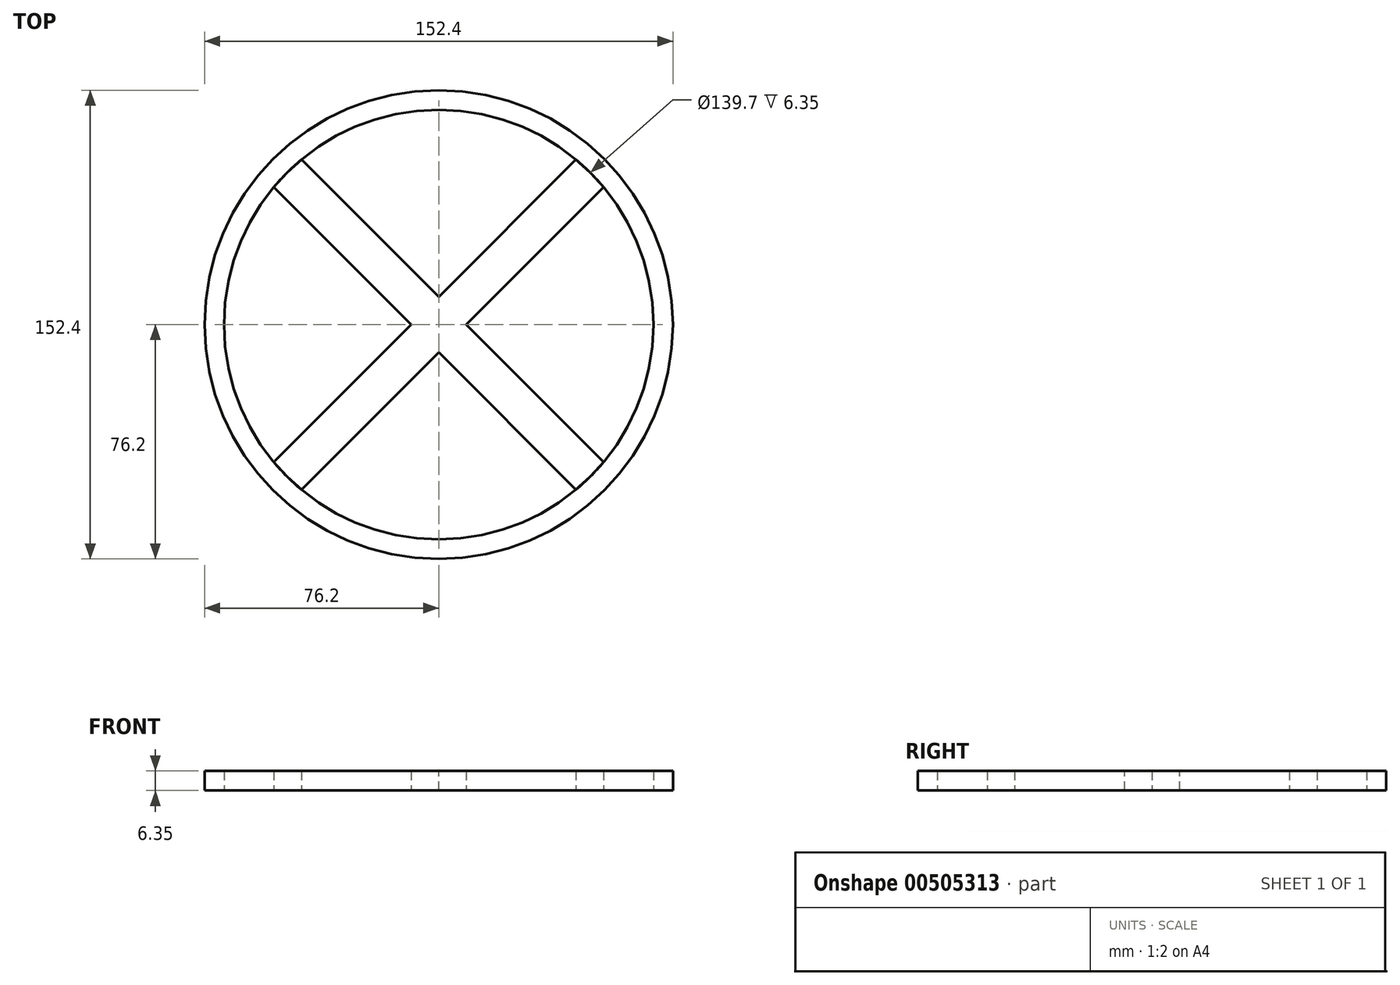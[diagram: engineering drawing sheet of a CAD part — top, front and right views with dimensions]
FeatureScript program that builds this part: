
annotation { "Feature Type Name" : "Feature", "Feature Type Description" : "" }
export const myFeature = defineFeature(function(context is Context, id is Id, definition is map)
    precondition{}
    {
        {
            var Q0;
            Q0=qCreatedBy(makeId("Top.planeOp"),FACE);
            var sketch = newSketch(context, id + "F0", { "sketchPlane" : qUnion([Q0])});
            skCircle(sketch, "E0", {"center": v(0, 0) * mm, "radius": 76.2 * mm});
            skCircle(sketch, "E1", {"center": v(0, 0) * mm, "radius": 69.85 * mm});
            skLineSegment(sketch, "E2", {"start": v(0, 0) * mm, "end": v(-76.2, 76.2) * mm});
            skLineSegment(sketch, "E3", {"start": v(0, 0) * mm, "end": v(75.1, 75.1) * mm});
            skLineSegment(sketch, "E4.MirrorCS", {"start": v(0, 0) * mm, "end": v(75.1, -75.1) * mm});
            skLineSegment(sketch, "E5.MirrorCS", {"start": v(0, 0) * mm, "end": v(-76.2, -76.2) * mm});
            skLineSegment(sketch, "E6.0", {"start": v(0, -8.98) * mm, "end": v(79.59, 70.6) * mm});
            skLineSegment(sketch, "E6.1", {"start": v(0, -8.98) * mm, "end": v(-80.68, 71.7) * mm});
            skLineSegment(sketch, "E7.0", {"start": v(0, 8.98) * mm, "end": v(70.6, 79.59) * mm});
            skLineSegment(sketch, "E7.1", {"start": v(0, 8.98) * mm, "end": v(-71.7, 80.68) * mm});
            skLineSegment(sketch, "E8.0", {"start": v(0, -8.98) * mm, "end": v(70.6, -79.59) * mm});
            skLineSegment(sketch, "E8.1", {"start": v(0, -8.98) * mm, "end": v(-71.7, -80.68) * mm});
            skLineSegment(sketch, "E9.0", {"start": v(0, 8.98) * mm, "end": v(79.59, -70.6) * mm});
            skLineSegment(sketch, "E9.1", {"start": v(0, 8.98) * mm, "end": v(-80.68, -71.7) * mm});
            skSolve(sketch);
        }
        {
            var Q0;
            {var subQ0=sQuery(id+"F0.wireOp",EDGE,"E7.1");var subQ1=sQuery(id+"F0.wireOp",EDGE,"E1");var subQ2=makeQuery(id+"F0.imprint","INTERSECT",VERTEX,{"derivedFrom":[subQ1,subQ0]});Q0=makeQuery(id+"F0.imprint","IMPRINT",FACE,{"disambiguationData":[TD([[makeQuery(id+"F0.imprint","IMPRINT",EDGE,{"disambiguationData":[TD([[subQ2,-1.0]])],"derivedFrom":subQ1}),1.0]])]});}
            var Q1;
            {var subQ0=sQuery(id+"F0.wireOp",EDGE,"E2");var subQ1=sQuery(id+"F0.wireOp",EDGE,"E1");var subQ2=makeQuery(id+"F0.imprint","INTERSECT",VERTEX,{"derivedFrom":[subQ1,subQ0]});Q1=makeQuery(id+"F0.imprint","IMPRINT",FACE,{"disambiguationData":[TD([[makeQuery(id+"F0.imprint","IMPRINT",EDGE,{"disambiguationData":[TD([[subQ2,-1.0]])],"derivedFrom":subQ1}),1.0]])]});}
            var Q2;
            {var subQ0=sQuery(id+"F0.wireOp",EDGE,"E9.1");var subQ1=sQuery(id+"F0.wireOp",EDGE,"E1");var subQ2=makeQuery(id+"F0.imprint","INTERSECT",VERTEX,{"derivedFrom":[subQ1,subQ0]});Q2=makeQuery(id+"F0.imprint","IMPRINT",FACE,{"disambiguationData":[TD([[makeQuery(id+"F0.imprint","IMPRINT",EDGE,{"disambiguationData":[TD([[subQ2,-1.0]])],"derivedFrom":subQ1}),1.0]])]});}
            var Q3;
            {var subQ0=sQuery(id+"F0.wireOp",EDGE,"E5.MirrorCS");var subQ1=sQuery(id+"F0.wireOp",EDGE,"E1");var subQ2=makeQuery(id+"F0.imprint","INTERSECT",VERTEX,{"derivedFrom":[subQ1,subQ0]});Q3=makeQuery(id+"F0.imprint","IMPRINT",FACE,{"disambiguationData":[TD([[makeQuery(id+"F0.imprint","IMPRINT",EDGE,{"disambiguationData":[TD([[subQ2,-1.0]])],"derivedFrom":subQ1}),1.0]])]});}
            var Q4;
            {var subQ1=sQuery(id+"F0.wireOp",EDGE,"E4.MirrorCS");var subQ3=sQuery(id+"F0.wireOp",EDGE,"E6.0");var subQ4=makeQuery(id+"F0.imprint","INTERSECT",VERTEX,{"derivedFrom":[subQ1,subQ3]});Q4=makeQuery(id+"F0.imprint","IMPRINT",FACE,{"disambiguationData":[TD([[makeQuery(id+"F0.imprint","IMPRINT",EDGE,{"disambiguationData":[TD([[subQ4,1.0]])],"derivedFrom":subQ1}),-1.0]])]});}
            var Q5;
            {var subQ0=sQuery(id+"F0.wireOp",EDGE,"E5.MirrorCS");var subQ5=sQuery(id+"F0.wireOp",EDGE,"E6.1");var subQ6=makeQuery(id+"F0.imprint","INTERSECT",VERTEX,{"derivedFrom":[subQ0,subQ5]});Q5=makeQuery(id+"F0.imprint","IMPRINT",FACE,{"disambiguationData":[TD([[makeQuery(id+"F0.imprint","IMPRINT",EDGE,{"disambiguationData":[TD([[subQ6,-1.0]])],"derivedFrom":subQ5}),-1.0]])]});}
            var Q6;
            {var subQ1=sQuery(id+"F0.wireOp",EDGE,"E2");var subQ3=sQuery(id+"F0.wireOp",EDGE,"E9.1");var subQ4=makeQuery(id+"F0.imprint","INTERSECT",VERTEX,{"derivedFrom":[subQ1,subQ3]});Q6=makeQuery(id+"F0.imprint","IMPRINT",FACE,{"disambiguationData":[TD([[makeQuery(id+"F0.imprint","IMPRINT",EDGE,{"disambiguationData":[TD([[subQ4,1.0]])],"derivedFrom":subQ1}),-1.0]])]});}
            var Q7;
            {var subQ0=sQuery(id+"F0.wireOp",EDGE,"E4.MirrorCS");var subQ5=sQuery(id+"F0.wireOp",EDGE,"E6.0");var subQ6=makeQuery(id+"F0.imprint","INTERSECT",VERTEX,{"derivedFrom":[subQ0,subQ5]});Q7=makeQuery(id+"F0.imprint","IMPRINT",FACE,{"disambiguationData":[TD([[makeQuery(id+"F0.imprint","IMPRINT",EDGE,{"disambiguationData":[TD([[subQ6,-1.0]])],"derivedFrom":subQ5}),1.0]])]});}
            var Q8;
            {var subQ0=sQuery(id+"F0.wireOp",EDGE,"E8.0");var subQ1=sQuery(id+"F0.wireOp",EDGE,"E1");var subQ2=makeQuery(id+"F0.imprint","INTERSECT",VERTEX,{"derivedFrom":[subQ1,subQ0]});Q8=makeQuery(id+"F0.imprint","IMPRINT",FACE,{"disambiguationData":[TD([[makeQuery(id+"F0.imprint","IMPRINT",EDGE,{"disambiguationData":[TD([[subQ2,-1.0]])],"derivedFrom":subQ1}),1.0]])]});}
            var Q9;
            {var subQ0=sQuery(id+"F0.wireOp",EDGE,"E4.MirrorCS");var subQ1=sQuery(id+"F0.wireOp",EDGE,"E1");var subQ2=makeQuery(id+"F0.imprint","INTERSECT",VERTEX,{"derivedFrom":[subQ1,subQ0]});Q9=makeQuery(id+"F0.imprint","IMPRINT",FACE,{"disambiguationData":[TD([[makeQuery(id+"F0.imprint","IMPRINT",EDGE,{"disambiguationData":[TD([[subQ2,-1.0]])],"derivedFrom":subQ1}),1.0]])]});}
            var Q10;
            {var subQ0=sQuery(id+"F0.wireOp",EDGE,"E3");var subQ1=sQuery(id+"F0.wireOp",EDGE,"E1");var subQ2=makeQuery(id+"F0.imprint","INTERSECT",VERTEX,{"derivedFrom":[subQ1,subQ0]});Q10=makeQuery(id+"F0.imprint","IMPRINT",FACE,{"disambiguationData":[TD([[makeQuery(id+"F0.imprint","IMPRINT",EDGE,{"disambiguationData":[TD([[subQ2,1.0]])],"derivedFrom":subQ1}),1.0]])]});}
            var Q11;
            {var subQ0=sQuery(id+"F0.wireOp",EDGE,"E3");var subQ1=sQuery(id+"F0.wireOp",EDGE,"E1");var subQ2=makeQuery(id+"F0.imprint","INTERSECT",VERTEX,{"derivedFrom":[subQ1,subQ0]});Q11=makeQuery(id+"F0.imprint","IMPRINT",FACE,{"disambiguationData":[TD([[makeQuery(id+"F0.imprint","IMPRINT",EDGE,{"disambiguationData":[TD([[subQ2,-1.0]])],"derivedFrom":subQ1}),1.0]])]});}
            extrude(context, id + "F1", {"entities" : qUnion([Q0, Q1, Q2, Q3, Q4, Q5, Q6, Q7, Q8, Q9, Q10, Q11]), "depth" : 6.35 * mm});
        }
        {
            var Q0;
            Q0 = qSketchRegion(id + "F0", true);
            extrude(context, id + "F2", {"entities" : qUnion([Q0]), "depth" : 6.35 * mm});
        }
        {
            var Q0;
            Q0=qCreatedBy(makeId("Top.planeOp"),FACE);
            var sketch = newSketch(context, id + "F3", { "sketchPlane" : qUnion([Q0])});
            skCircle(sketch, "E10", {"center": v(0, 0) * mm, "radius": 69.85 * mm});
            skSolve(sketch);
        }
        {
            var Q0;
            Q0 = qSketchRegion(id + "F3", true);
            extrude(context, id + "F4", {"entities" : qUnion([Q0]), "depth" : 0.03 * mm});
        }
    });
